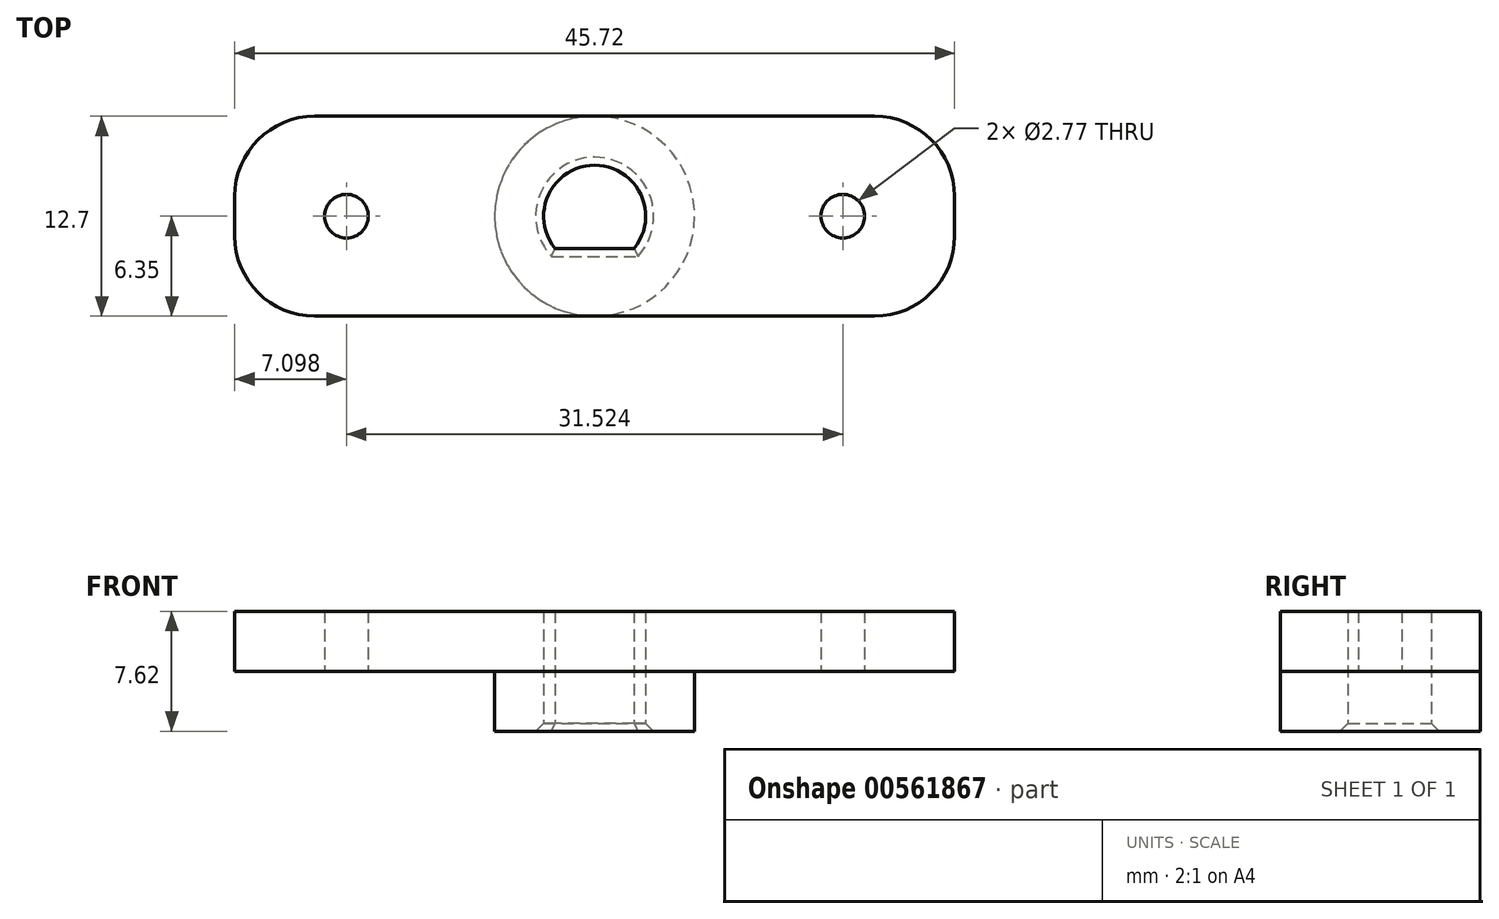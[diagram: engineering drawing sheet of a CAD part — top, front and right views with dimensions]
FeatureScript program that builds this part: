
annotation { "Feature Type Name" : "Feature", "Feature Type Description" : "" }
export const myFeature = defineFeature(function(context is Context, id is Id, definition is map)
    precondition{}
    {
        {
            var Q0;
            Q0=qCreatedBy(makeId("Top.planeOp"),FACE);
            var sketch = newSketch(context, id + "F0", { "sketchPlane" : qUnion([Q0])});
            skLineSegment(sketch, "E0.bottom", {"start": v(-22.86, 0) * mm, "end": v(22.86, 0) * mm});
            skLineSegment(sketch, "E0.top", {"start": v(-22.86, 12.7) * mm, "end": v(22.86, 12.7) * mm});
            skLineSegment(sketch, "E0.left", {"start": v(-22.86, 0) * mm, "end": v(-22.86, 12.7) * mm});
            skLineSegment(sketch, "E0.right", {"start": v(22.86, 0) * mm, "end": v(22.86, 12.7) * mm});
            skCircle(sketch, "E1", {"center": v(0, 6.35) * mm, "radius": 3.24 * mm});
            skLineSegment(sketch, "E2", {"start": v(-2.51, 4.3) * mm, "end": v(2.51, 4.3) * mm});
            skCircle(sketch, "E3", {"center": v(15.76, 6.35) * mm, "radius": 1.38 * mm});
            skCircle(sketch, "E4.MirrorC", {"center": v(-15.76, 6.35) * mm, "radius": 1.38 * mm});
            skSolve(sketch);
        }
        {
            var Q0;
            Q0=makeQuery(id+"F0.imprint","IMPRINT",FACE,{"disambiguationData":[TD([[makeQuery(id+"F0.imprint","IMPRINT",EDGE,{"derivedFrom":sQuery(id+"F0.wireOp",EDGE,"E0.bottom")}),1.0]])]});
            var Q1;
            {var subQ0=sQuery(id+"F0.wireOp",EDGE,"E2");Q1=makeQuery(id+"F0.imprint","IMPRINT",FACE,{"disambiguationData":[TD([[makeQuery(id+"F0.imprint","IMPRINT",EDGE,{"derivedFrom":subQ0}),-1.0]])]});}
            var Q2;
            {var subQ0=sQuery(id+"F0.wireOp",EDGE,"E2");Q2=makeQuery(id+"F0.imprint","IMPRINT",FACE,{"disambiguationData":[TD([[makeQuery(id+"F0.imprint","IMPRINT",EDGE,{"derivedFrom":subQ0}),1.0]])]});}
            extrude(context, id + "F1", {"entities" : qUnion([Q0, Q1, Q2]), "depth" : 3.8 * mm, "offsetDistance" : 25.4 * mm});
        }
        {
            var Q0;
            Q0=makeQuery(id+"F1.opExtrude","SWEPT_EDGE",EDGE,{"disambiguationData":[OSD([sQuery(id+"F0.wireOp",EDGE,"E0.top"),sQuery(id+"F0.wireOp",EDGE,"E0.left")])]});
            var Q1;
            Q1=makeQuery(id+"F1.opExtrude","SWEPT_EDGE",EDGE,{"disambiguationData":[OSD([sQuery(id+"F0.wireOp",EDGE,"E0.bottom"),sQuery(id+"F0.wireOp",EDGE,"E0.left")])]});
            var Q2;
            Q2=makeQuery(id+"F1.opExtrude","SWEPT_EDGE",EDGE,{"disambiguationData":[OSD([sQuery(id+"F0.wireOp",EDGE,"E0.top"),sQuery(id+"F0.wireOp",EDGE,"E0.right")])]});
            var Q3;
            Q3=makeQuery(id+"F1.opExtrude","SWEPT_EDGE",EDGE,{"disambiguationData":[OSD([sQuery(id+"F0.wireOp",EDGE,"E0.bottom"),sQuery(id+"F0.wireOp",EDGE,"E0.right")])]});
            fillet(context, id + "F2", {"entities" : qUnion([Q0, Q1, Q2, Q3]), "radius" : 5.08 * mm, "tangentPropagation" : true, "allowEdgeOverflow" : false});
        }
        {
            var Q0;
            Q0=makeQuery(id+"F1.opExtrude","CAP_FACE",FACE,{"disambiguationData":[OSD([sQuery(id+"F0.wireOp",EDGE,"E0.bottom"),sQuery(id+"F0.wireOp",EDGE,"E0.top"),sQuery(id+"F0.wireOp",EDGE,"E0.left"),sQuery(id+"F0.wireOp",EDGE,"E0.right"),sQuery(id+"F0.wireOp",EDGE,"E3"),sQuery(id+"F0.wireOp",EDGE,"E4.MirrorC")])],"isStart":true});
            var sketch = newSketch(context, id + "F3", { "sketchPlane" : qUnion([Q0])});
            skCircle(sketch, "E5", {"center": v(0, -6.35) * mm, "radius": 6.35 * mm});
            skSolve(sketch);
        }
        {
            var Q0;
            {var subQ0=sQuery(id+"F3.wireOp",EDGE,"E5");var subQ1=makeQuery(id+"F3.imprint","INTERSECT",VERTEX,{"derivedFrom":[makeQuery(id+"F1.opExtrude","CAP_EDGE",EDGE,{"disambiguationData":[OSD([sQuery(id+"F0.wireOp",EDGE,"E0.bottom")])],"isStart":true}),subQ0]});Q0=makeQuery(id+"F3.imprint","IMPRINT",FACE,{"disambiguationData":[TD([[makeQuery(id+"F3.imprint","IMPRINT",EDGE,{"disambiguationData":[TD([[subQ1,-1.0]])],"derivedFrom":subQ0}),1.0]])]});}
            extrude(context, id + "F4", {"entities" : qUnion([Q0]), "operationType" : NewBodyOperationType.ADD, "depth" : 3.8 * mm, "offsetDistance" : 25.4 * mm});
        }
        {
            var Q0;
            {var subQ0=sQuery(id+"F0.wireOp",EDGE,"E2");Q0=makeQuery(id+"F0.imprint","IMPRINT",FACE,{"disambiguationData":[TD([[makeQuery(id+"F0.imprint","IMPRINT",EDGE,{"derivedFrom":subQ0}),1.0]])]});}
            extrude(context, id + "F5", {"entities" : qUnion([Q0]), "operationType" : NewBodyOperationType.REMOVE, "endBound" : BoundingType.SYMMETRIC, "depth" : 25.4 * mm, "offsetDistance" : 25.4 * mm});
        }
        {
            var Q0;
            Q0=makeQuery(id+"F5.boolean.opBoolean","INTERSECT",EDGE,{"derivedFrom":[makeQuery(id+"F4.opExtrude","CAP_FACE",FACE,{"disambiguationData":[OSD([sQuery(id+"F3.wireOp",EDGE,"E5")])],"isStart":false}),makeQuery(id+"F5.opExtrude","SWEPT_FACE",FACE,{"disambiguationData":[OSD([sQuery(id+"F0.wireOp",EDGE,"E2")])]})]});
            var Q1;
            Q1=makeQuery(id+"F5.boolean.opBoolean","INTERSECT",EDGE,{"derivedFrom":[makeQuery(id+"F4.opExtrude","CAP_FACE",FACE,{"disambiguationData":[OSD([sQuery(id+"F3.wireOp",EDGE,"E5")])],"isStart":false}),makeQuery(id+"F5.opExtrude","SWEPT_FACE",FACE,{"disambiguationData":[OSD([sQuery(id+"F0.wireOp",EDGE,"E1")])]})]});
            chamfer(context, id + "F6", {"entities" : qUnion([Q0, Q1]), "width" : 0.5 * mm, "tangentPropagation" : true});
        }
    });
